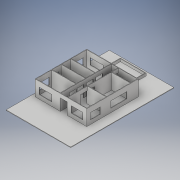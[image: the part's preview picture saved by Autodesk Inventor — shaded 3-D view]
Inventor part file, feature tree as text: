
AUTODESK INVENTOR PART (.ipt)
format: ipt  version: 2019 (Build 230136000, 136)  size: 356,352 bytes
history: native  units: mm
features: extrude x14, sketch x14, plane x2, other x1
ambient origin geometry x8: Origin, YZ Plane, XZ Plane, XY Plane, X Axis, Y Axis, Z Axis, Center Point
bodies: Body1 (feature_tree)
feature tree (31):
  other  "Sólido1"
  extrude  "Extrusión1"  Depth=800.0mm
  sketch  "Boceto2"  dims[d2=4.0mm d3=0.0mm d4=400.0mm]
  plane  "Plano de trabajo1"
  extrude  "Extrusión3"  Depth=400.0mm
  plane  "Plano de trabajo2"
  sketch  "Boceto4"  dims[d7=75.0mm d8=400.0mm]
  extrude  "Extrusión4"  Depth=200.0mm
  extrude  "Extrusión5"  Depth=400.0mm
  extrude  "Extrusión6"  Depth=75.0mm
  extrude  "Extrusión7"  Depth=4.0mm
  extrude  "Extrusión8"  Depth=4.0mm
  extrude  "Extrusión9"  Depth=4.0mm
  extrude  "Extrusión10"  Depth=145.0mm
  extrude  "Extrusión11"  Depth=120.0mm
  extrude  "Extrusión12"  Depth=4.0mm
  extrude  "Extrusión13"  Depth=4.0mm
  extrude  "Extrusión14"  Depth=4.0mm
  extrude  "Extrusión15"  Depth=120.0mm TaperAngle=0.0deg
  sketch  "Boceto1"  dims[d0=500.0mm d1=800.0mm]
  sketch  "Boceto3"  dims[d5=400.0mm d6=200.0mm]
  sketch  "Boceto5"  dims[d9=400.0mm d10=75.0mm]
  sketch  "Boceto6"  dims[d11=200.0mm d12=4.0mm]
  sketch  "Boceto7"  dims[d13=4.0mm d14=4.0mm]
  sketch  "Boceto8"  dims[d15=4.0mm d16=4.0mm]
  sketch  "Boceto9"  dims[d17=60.0mm d18=145.0mm]
  sketch  "Boceto10"  dims[d19=150.0mm d20=120.0mm]
  sketch  "Boceto11"  dims[d21=120.0mm d22=4.0mm]
  sketch  "Boceto12"  dims[d23=4.0mm d24=2.0mm]
  sketch  "Boceto13"  dims[d25=4.0mm d27=4.0mm]
  sketch  "Boceto14"  dims[d31=90.0mm d32=120.0mm d33=0.0mm d34=52.0mm d35=90.0mm d36=52.0mm d37=52.0mm d38=52.0mm d39=52.0mm d40=4.0mm d41=120.0mm d42=0.0mm d43=120.0mm d44=0.0mm d45=52.0mm d46=90.0mm d47=52.0mm d48=52.0mm d49=120.0mm d50=0.0mm d51=90.0mm d52=120.0mm d53=0.0mm d54=200.0mm d55=130.0mm d56=40.0mm d57=115.0mm d58=192.0mm d59=122.0mm d60=4.0mm d61=4.0mm d62=20.0mm d63=0.0mm d64=100.0mm d65=50.0mm d66=30.0mm d67=30.0mm d68=10.0mm d69=0.0mm d70=75.0mm d71=50.0mm d72=30.0mm d73=30.0mm d74=10.0mm d75=0.0mm d76=75.0mm d77=50.0mm d78=30.0mm d79=30.0mm d80=35.0mm d81=50.0mm d82=30.0mm d83=17.5mm d84=10.0mm d85=0.0mm d86=90.0mm d88=30.0mm d89=50.0mm d90=30.0mm d91=10.0mm d92=0.0mm d93=100.0mm d94=50.0mm d95=30.0mm d96=30.0mm d97=10.0mm d98=0.0mm d99=10.0mm d100=0.0mm d101=125.0mm d102=50.0mm d103=30.0mm d105=91.0mm d106=10.0mm d107=0.0mm d108=0.0mm]
